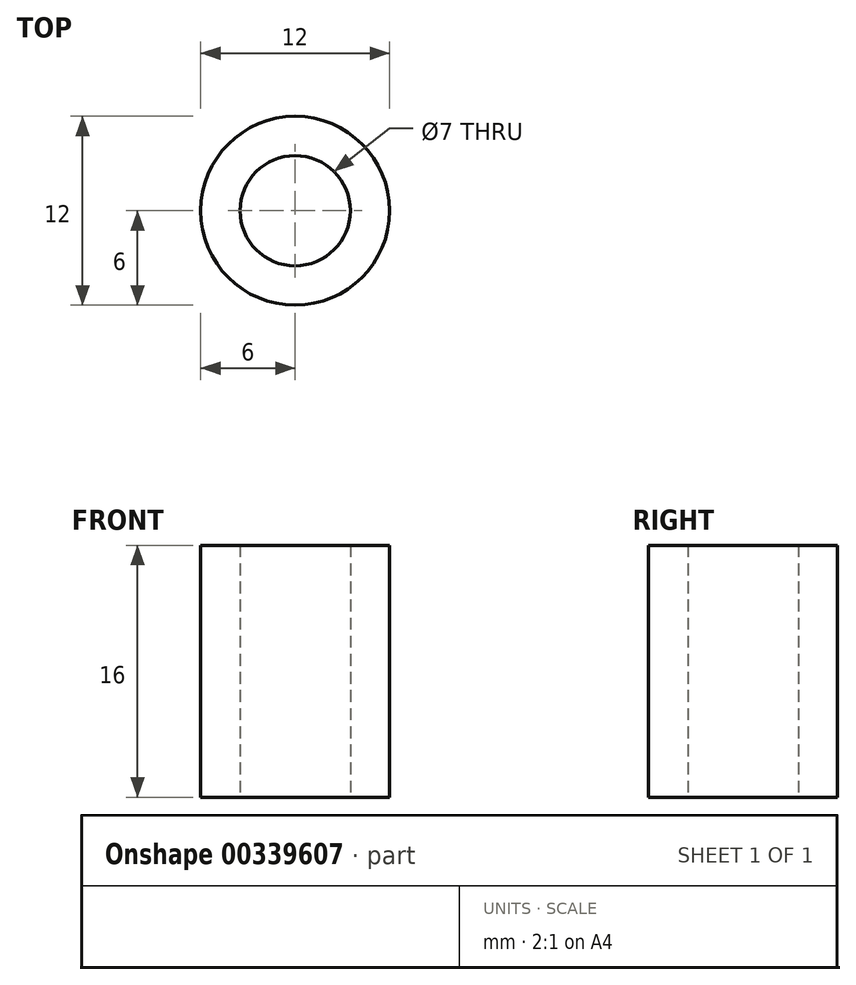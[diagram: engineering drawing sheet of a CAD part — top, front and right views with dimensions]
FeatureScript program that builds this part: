
annotation { "Feature Type Name" : "Feature", "Feature Type Description" : "" }
export const myFeature = defineFeature(function(context is Context, id is Id, definition is map)
    precondition{}
    {
        {
            var Q0;
            Q0=qCreatedBy(makeId("Top.planeOp"),FACE);
            var sketch = newSketch(context, id + "F0", { "sketchPlane" : qUnion([Q0])});
            skCircle(sketch, "E0", {"center": v(0, 0) * mm, "radius": 3.5 * mm});
            skCircle(sketch, "E1", {"center": v(0, 0) * mm, "radius": 6 * mm});
            skSolve(sketch);
        }
        {
            var Q0;
            Q0=qSketchRegion(id+"F0",true);
            extrude(context, id + "F1", {"entities" : qUnion([Q0]), "depth" : 16 * mm});
        }
    });
